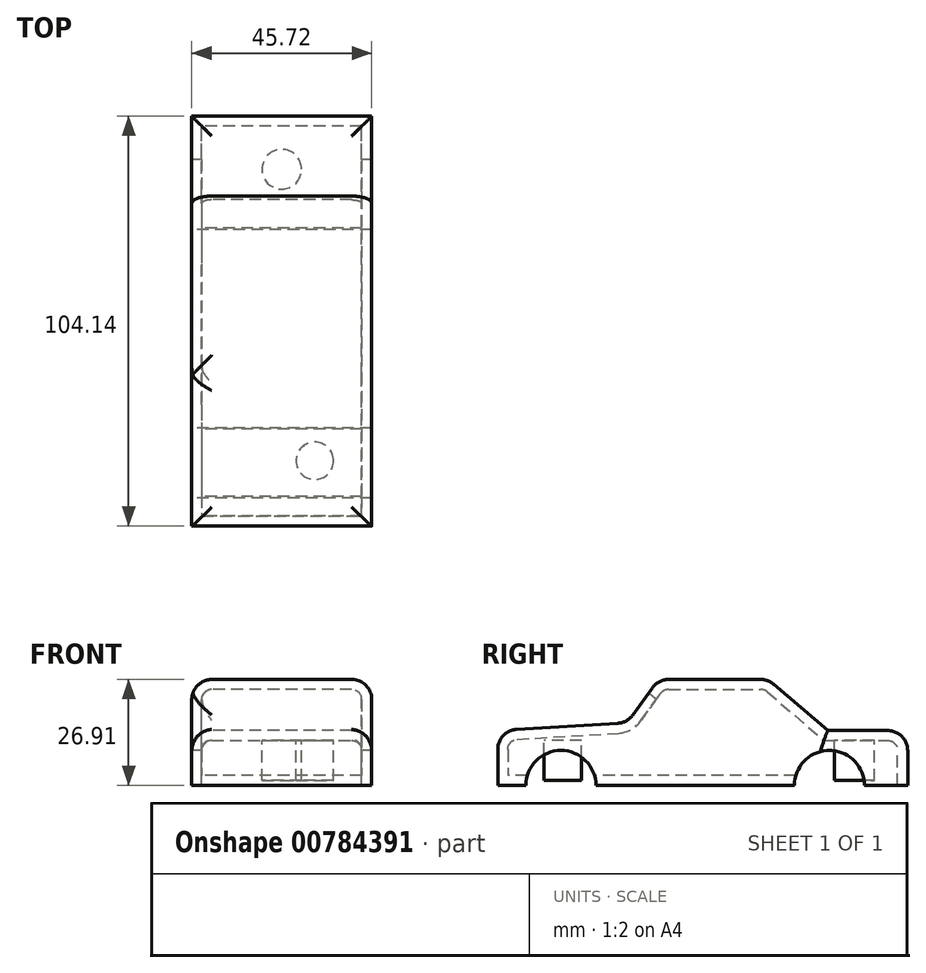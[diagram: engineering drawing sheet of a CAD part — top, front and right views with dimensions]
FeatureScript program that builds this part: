
annotation { "Feature Type Name" : "Feature", "Feature Type Description" : "" }
export const myFeature = defineFeature(function(context is Context, id is Id, definition is map)
    precondition{}
    {
        {
            var Q0;
            Q0=qCreatedBy(makeId("Right.planeOp"),FACE);
            var sketch = newSketch(context, id + "F0", { "sketchPlane" : qUnion([Q0])});
            skLineSegment(sketch, "E0", {"start": v(0, 0) * mm, "end": v(-59.54, 0) * mm});
            skLineSegment(sketch, "E1", {"start": v(-59.54, 0) * mm, "end": v(44.6, 0) * mm});
            skLineSegment(sketch, "E2", {"start": v(44.6, 0) * mm, "end": v(44.6, 13.94) * mm});
            skLineSegment(sketch, "E3", {"start": v(44.6, 13.94) * mm, "end": v(24.28, 13.94) * mm});
            skLineSegment(sketch, "E4", {"start": v(24.28, 13.94) * mm, "end": v(9.19, 26.91) * mm});
            skLineSegment(sketch, "E5", {"start": v(9.19, 26.91) * mm, "end": v(-18.75, 26.91) * mm});
            skLineSegment(sketch, "E6", {"start": v(-18.75, 26.91) * mm, "end": v(-26.58, 15.96) * mm});
            skLineSegment(sketch, "E7", {"start": v(-26.58, 15.96) * mm, "end": v(-59.54, 13.94) * mm});
            skLineSegment(sketch, "E8", {"start": v(-59.54, 13.94) * mm, "end": v(-59.54, 0) * mm});
            skCircle(sketch, "E9", {"center": v(-43.47, 0) * mm, "radius": 8.9 * mm});
            skCircle(sketch, "E10", {"center": v(24.72, 0) * mm, "radius": 8.9 * mm});
            skSolve(sketch);
        }
        {
            var Q0;
            {var subQ4=sQuery(id+"F0.wireOp",EDGE,"E2");Q0=makeQuery(id+"F0.imprint","IMPRINT",FACE,{"disambiguationData":[TD([[makeQuery(id+"F0.imprint","IMPRINT",EDGE,{"derivedFrom":subQ4}),1.0]])]});}
            extrude(context, id + "F1", {"entities" : qUnion([Q0]), "endBound" : BoundingType.SYMMETRIC, "depth" : 45.72 * mm, "offsetDistance" : 25.4 * mm});
        }
        {
            var Q0;
            Q0=makeQuery(id+"F1.opExtrude","CAP_EDGE",EDGE,{"disambiguationData":[OSD([sQuery(id+"F0.wireOp",EDGE,"E7")])],"isStart":false});
            var Q1;
            Q1=makeQuery(id+"F1.opExtrude","CAP_EDGE",EDGE,{"disambiguationData":[OSD([sQuery(id+"F0.wireOp",EDGE,"E6")])],"isStart":false});
            var Q2;
            Q2=makeQuery(id+"F1.opExtrude","CAP_EDGE",EDGE,{"disambiguationData":[OSD([sQuery(id+"F0.wireOp",EDGE,"E5")])],"isStart":false});
            var Q3;
            Q3=makeQuery(id+"F1.opExtrude","CAP_EDGE",EDGE,{"disambiguationData":[OSD([sQuery(id+"F0.wireOp",EDGE,"E4")])],"isStart":false});
            var Q4;
            Q4=makeQuery(id+"F1.opExtrude","CAP_EDGE",EDGE,{"disambiguationData":[OSD([sQuery(id+"F0.wireOp",EDGE,"E3")])],"isStart":false});
            var Q5;
            Q5=makeQuery(id+"F1.opExtrude","SWEPT_EDGE",EDGE,{"disambiguationData":[OSD([sQuery(id+"F0.wireOp",EDGE,"E2"),sQuery(id+"F0.wireOp",EDGE,"E3")])]});
            var Q6;
            Q6=makeQuery(id+"F1.opExtrude","CAP_EDGE",EDGE,{"disambiguationData":[OSD([sQuery(id+"F0.wireOp",EDGE,"E4")])],"isStart":true});
            var Q7;
            Q7=makeQuery(id+"F1.opExtrude","CAP_EDGE",EDGE,{"disambiguationData":[OSD([sQuery(id+"F0.wireOp",EDGE,"E5")])],"isStart":true});
            var Q8;
            Q8=makeQuery(id+"F1.opExtrude","CAP_EDGE",EDGE,{"disambiguationData":[OSD([sQuery(id+"F0.wireOp",EDGE,"E3")])],"isStart":true});
            var Q9;
            Q9=makeQuery(id+"F1.opExtrude","CAP_EDGE",EDGE,{"disambiguationData":[OSD([sQuery(id+"F0.wireOp",EDGE,"E7")])],"isStart":true});
            var Q10;
            Q10=makeQuery(id+"F1.opExtrude","SWEPT_EDGE",EDGE,{"disambiguationData":[OSD([sQuery(id+"F0.wireOp",EDGE,"E5"),sQuery(id+"F0.wireOp",EDGE,"E6")])]});
            var Q11;
            Q11=makeQuery(id+"F1.opExtrude","SWEPT_EDGE",EDGE,{"disambiguationData":[OSD([sQuery(id+"F0.wireOp",EDGE,"E4"),sQuery(id+"F0.wireOp",EDGE,"E5")])]});
            var Q12;
            Q12=makeQuery(id+"F1.opExtrude","SWEPT_EDGE",EDGE,{"disambiguationData":[OSD([sQuery(id+"F0.wireOp",EDGE,"E6"),sQuery(id+"F0.wireOp",EDGE,"E7")])]});
            var Q13;
            Q13=makeQuery(id+"F1.opExtrude","SWEPT_EDGE",EDGE,{"disambiguationData":[OSD([sQuery(id+"F0.wireOp",EDGE,"E7"),sQuery(id+"F0.wireOp",EDGE,"E8")])]});
            fillet(context, id + "F2", {"entities" : qUnion([Q0, Q1, Q2, Q3, Q4, Q5, Q6, Q7, Q8, Q9, Q10, Q11, Q12, Q13]), "radius" : 5.08 * mm, "tangentPropagation" : true, "allowEdgeOverflow" : false});
        }
        {
            var Q0;
            {var subQ0=sQuery(id+"F0.wireOp",EDGE,"E1");Q0=makeQuery(id+"F1.opExtrude","SWEPT_FACE",FACE,{"disambiguationData":[OSD([subQ0]),TDD([makeQuery(id+"F0.imprint","IMPRINT",EDGE,{"disambiguationData":[TD([[makeQuery(id+"F0.imprint","INTERSECT",VERTEX,{"disambiguationData":[OD(1.0)],"derivedFrom":[subQ0,sQuery(id+"F0.wireOp",EDGE,"E9")]}),-1.0]])],"derivedFrom":subQ0})])]});}
            var Q1;
            Q1=makeQuery(id+"F1.opExtrude","SWEPT_FACE",FACE,{"disambiguationData":[OSD([sQuery(id+"F0.wireOp",EDGE,"E9")])]});
            var Q2;
            {var subQ0=sQuery(id+"F0.wireOp",EDGE,"E1");Q2=makeQuery(id+"F1.opExtrude","SWEPT_FACE",FACE,{"disambiguationData":[OSD([subQ0]),TDD([makeQuery(id+"F0.imprint","IMPRINT",EDGE,{"disambiguationData":[TD([[makeQuery(id+"F0.imprint","INTERSECT",VERTEX,{"derivedFrom":[subQ0,sQuery(id+"F0.wireOp",EDGE,"E8")]}),-1.0]])],"derivedFrom":subQ0})])]});}
            var Q3;
            Q3=makeQuery(id+"F1.opExtrude","SWEPT_FACE",FACE,{"disambiguationData":[OSD([sQuery(id+"F0.wireOp",EDGE,"E10")])]});
            var Q4;
            {var subQ0=sQuery(id+"F0.wireOp",EDGE,"E1");Q4=makeQuery(id+"F1.opExtrude","SWEPT_FACE",FACE,{"disambiguationData":[OSD([subQ0]),TDD([makeQuery(id+"F0.imprint","IMPRINT",EDGE,{"disambiguationData":[TD([[makeQuery(id+"F0.imprint","INTERSECT",VERTEX,{"derivedFrom":[subQ0,sQuery(id+"F0.wireOp",EDGE,"E2")]}),1.0]])],"derivedFrom":subQ0})])]});}
            shell(context, id + "F3", {"entities" : qUnion([Q0, Q1, Q2, Q3, Q4]), "thickness" : 2.54 * mm});
        }
        {
            var Q0;
            {var subQ0=sQuery(id+"F0.wireOp",EDGE,"E3");Q0=makeQuery(id+"F3.opShell","OFFSET_FACE",FACE,{"disambiguationData":[OSD([subQ0]),TDD([makeQuery(id+"F1.opExtrude","SWEPT_FACE",FACE,{"disambiguationData":[OSD([subQ0])]})])]});}
            var sketch = newSketch(context, id + "F4", { "sketchPlane" : qUnion([Q0])});
            skCircle(sketch, "E11", {"center": v(8.38, 42.98) * mm, "radius": 4.77 * mm});
            skCircle(sketch, "E12", {"center": v(0, -31.09) * mm, "radius": 5.05 * mm});
            skPoint(sketch, "E12.centerSnap0", {"position": v(0, -39.52) * mm});
            skCircle(sketch, "E13.MirrorC", {"center": v(-8.38, 42.98) * mm, "radius": 4.77 * mm});
            skSolve(sketch);
        }
        {
            var Q0;
            Q0=makeQuery(id+"F4.imprint","IMPRINT",FACE,{"disambiguationData":[TD([[makeQuery(id+"F4.imprint","IMPRINT",EDGE,{"derivedFrom":sQuery(id+"F4.wireOp",EDGE,"E12")}),1.0]])]});
            var Q1;
            Q1=makeQuery(id+"F4.imprint","IMPRINT",FACE,{"disambiguationData":[TD([[makeQuery(id+"F4.imprint","IMPRINT",EDGE,{"derivedFrom":sQuery(id+"F4.wireOp",EDGE,"E13.MirrorC")}),-1.0]])]});
            var Q2;
            Q2=makeQuery(id+"F4.imprint","IMPRINT",FACE,{"disambiguationData":[TD([[makeQuery(id+"F4.imprint","IMPRINT",EDGE,{"derivedFrom":sQuery(id+"F4.wireOp",EDGE,"E11")}),1.0]])]});
            var Q3;
            Q3=sQuery(id+"F4.wireOp",EDGE,"E13.MirrorC");
            var Q4;
            Q4=sQuery(id+"F4.wireOp",EDGE,"E11");
            var Q5;
            Q5=sQuery(id+"F4.wireOp",EDGE,"E12");
            extrude(context, id + "F5", {"entities" : qUnion([Q0, Q1, Q2]), "operationType" : NewBodyOperationType.ADD, "surfaceEntities" : qUnion([Q3, Q4, Q5]), "depth" : 10.16 * mm, "offsetDistance" : 25.4 * mm});
        }
    });
